# Revit family: Door-NanaWall-Cero_II-Unit_W
name_source: partatom
category: Doors
revit_build: Autodesk Revit Architecture 2014 (Build: 20140709_2115(x64)
units: mm (PartAtom-declared; Revit-internal decimal feet)

## types (4) — shared parameters
Actual Height = 7' - 0"
Actual Panel Width = 2' - 0"
Actual Width = 4' - 2 193/256"
Analytic Construction = Metal frame, double/triple glass, glass storm
C to Ext = 0' - 6 3/128"
C to Int = 0' - 2 163/256"
Construction Type = New Construction
Description = Sliding Glass Wall - PXXP Configuration
Elevation D = No
Finish = Metal - Nanawall - Clear (anodized)
Function = Exterior
Glass Lite Thickness = 0' - 0 1/4"
Glazing Material = Glass - NanaWall - Generic
Glazing Thickness = 0' - 1 107/256"
Half Thickness = 0' - 0 3/8"
Heat Transfer Coefficient (U) = 0.49 BTU/(h·ft²·°F)
Height = 7' - 0"
Height C = 7' - 0"
Inset Note = To set Door into wall use Inset parameter found in Instance Properties.
Installation and Service URL = https://www.nanawall.com
Manufacturer = NanaWall
Manufacturer Fax Number = (415) 383-0312
Model = Cero II - Unit W
Operation = Sliding
Panel Width = 2' - 0"
Panel Width C = 2' - 0"
Performance URL = https://www.nanawall.com
Pocket Length = 2' - 0"
Product Name = Cero
Product Page URL = https://www.nanawall.com
Rough Height = 7' - 0 1/2"
Rough Offset = 0' - 0 1/2"
Rough Width = 4' - 3 193/256"
S Glazing = 0' - 0 111/128"
Sill Width C = 8' - 2 193/256"
Size Note = Contact Nanawall for Larger Sizes
Sizing Statement = Maximum Panel Size = 7' 4 1/2 (W) x 13' 1 (H) (2250 mm x 4000 mm)
Subcategory = Sliding Glass Wall
Thermal Resistance (R) = 2.0409 (h·ft²·°F)/BTU
Thickness = 0' - 0 3/4"
Top Glazing = 0' - 3 25/32"
URL = https://www.nanawall.com
Version = 2014-v1.0a
Wall Closure = By host
Warranty URL = https://www.nanawall.com
Width = 4' - 2 193/256"
Width C = 4' - 2 193/256"
zero-valued in all types: Solar Heat Gain Coefficient, Visual Light Transmittance

## per-type parameters (varying)
| type | Bottom Glazing | Bottom Sash | Flush Saddle Hybrid Sill | Flush Sill | Higher Weather Performance Sill | Low Profile Saddle Sill | Low Sills | Panel Height | Sill Height |
| Cero_II-Unit_W-PXXP_Configuration Higher Weather Performance Sill | 0' - 3 25/32" | 0' - 2 31/128" | No | No | Yes | No | No | 6' - 7 33/64" | 0' - 2 61/64" |
| Cero_II-Unit_W-PXXP_Configuration Flush Sill | 0' - 1 103/128" | 0' - 0 49/256" | No | Yes | No | No | Yes | 6' - 9 145/256" | 0' - 0" |
| Cero_II-Unit_W-PXXP_Configuration Flush Saddle Hybrid Sill | 0' - 2 71/256" | 0' - 0 95/128" | Yes | No | No | No | Yes | 6' - 9 1/64" | 0' - 0 141/256" |
| Cero_II-Unit_W-PXXP_Configuration Low Profile Saddle Sill | 0' - 2 71/256" | 0' - 0 95/128" | No | No | No | Yes | Yes | 6' - 9 1/64" | 0' - 0 141/256" |

## geometry (parser evidence)
native form markers: Blend x870, Sweep x14
no freeform markers — native parametric forms only
